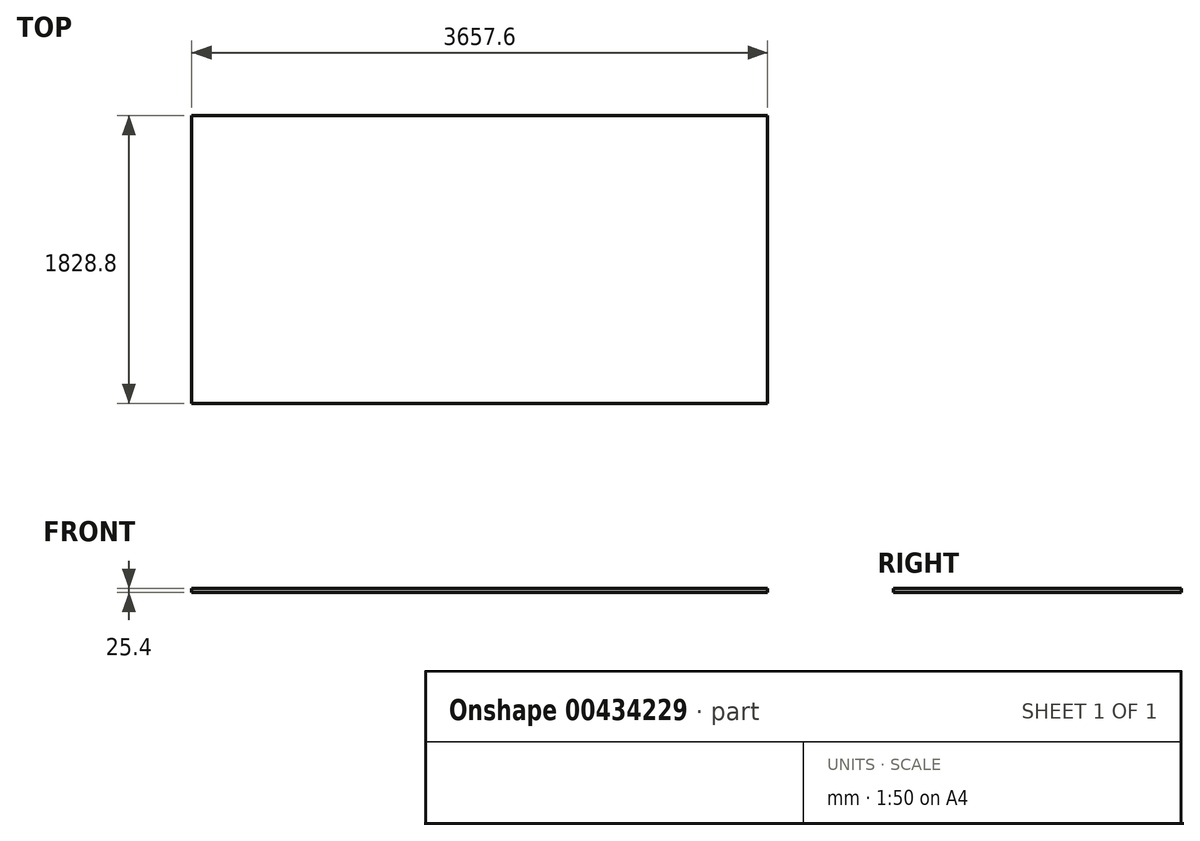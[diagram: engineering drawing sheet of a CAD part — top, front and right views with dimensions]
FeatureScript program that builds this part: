
annotation { "Feature Type Name" : "Feature", "Feature Type Description" : "" }
export const myFeature = defineFeature(function(context is Context, id is Id, definition is map)
    precondition{}
    {
        {
            var Q0;
            Q0=qCreatedBy(makeId("Top.planeOp"),FACE);
            var sketch = newSketch(context, id + "F0", { "sketchPlane" : qUnion([Q0])});
            skLineSegment(sketch, "E0.bottom", {"start": v(0, 0) * mm, "end": v(3657.6, 0) * mm});
            skLineSegment(sketch, "E0.top", {"start": v(0, 1828.8) * mm, "end": v(3657.6, 1828.8) * mm});
            skLineSegment(sketch, "E0.left", {"start": v(0, 0) * mm, "end": v(0, 1828.8) * mm});
            skLineSegment(sketch, "E0.right", {"start": v(3657.6, 0) * mm, "end": v(3657.6, 1828.8) * mm});
            skSolve(sketch);
        }
        {
            var Q0;
            Q0 = qSketchRegion(id + "F0", true);
            extrude(context, id + "F1", {"entities" : qUnion([Q0]), "depth" : 25.4 * mm});
        }
    });
